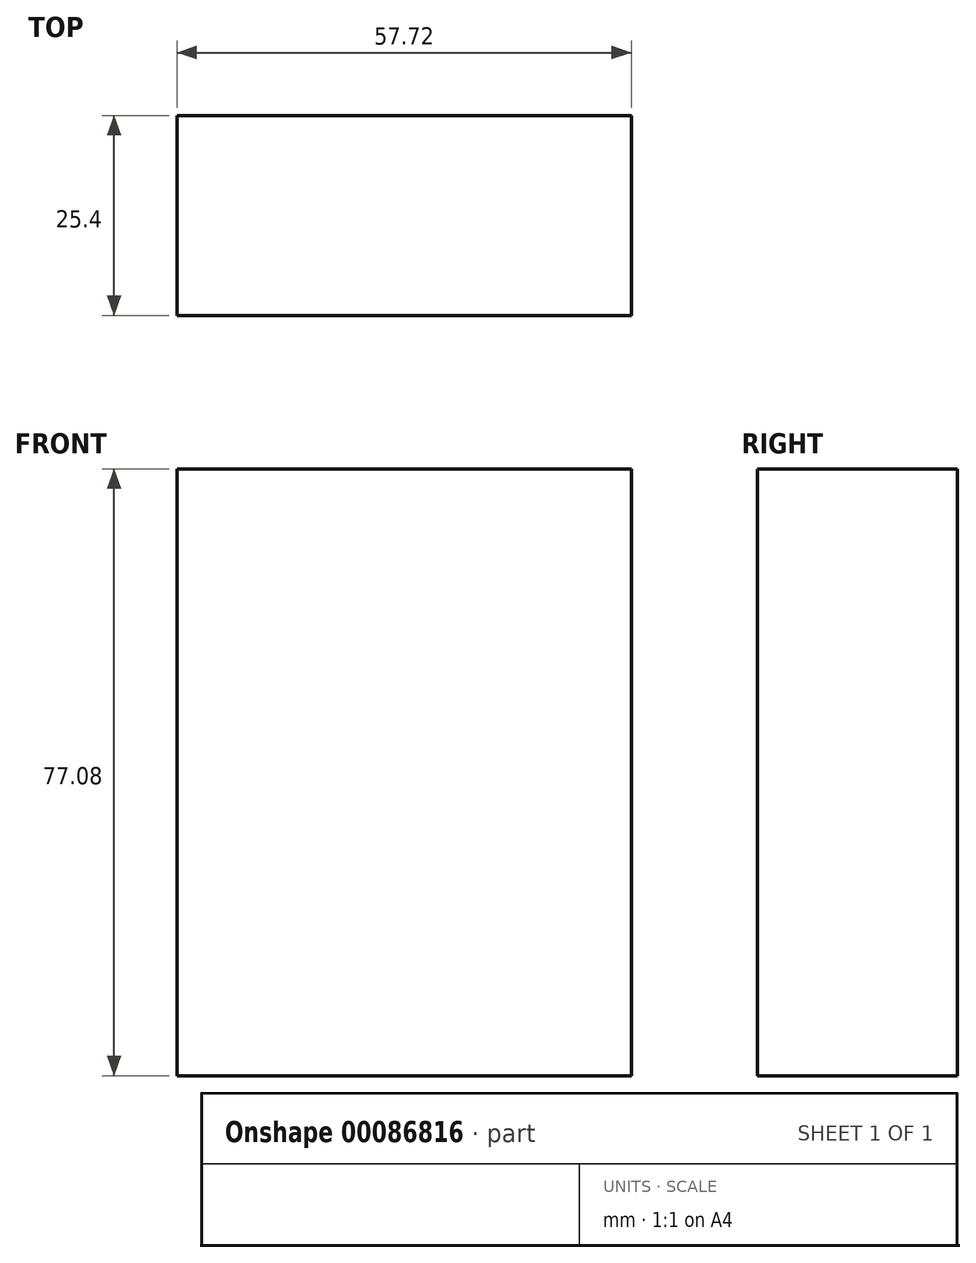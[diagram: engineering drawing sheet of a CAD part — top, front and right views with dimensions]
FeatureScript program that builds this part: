
annotation { "Feature Type Name" : "Feature", "Feature Type Description" : "" }
export const myFeature = defineFeature(function(context is Context, id is Id, definition is map)
    precondition{}
    {
        {
            var Q0;
            Q0=qCreatedBy(makeId("Front.planeOp"),FACE);
            var sketch = newSketch(context, id + "F0", { "sketchPlane" : qUnion([Q0])});
            skLineSegment(sketch, "E0.bottom", {"start": v(-28.86, -38.54) * mm, "end": v(28.86, -38.54) * mm});
            skLineSegment(sketch, "E0.top", {"start": v(-28.86, 38.54) * mm, "end": v(28.86, 38.54) * mm});
            skLineSegment(sketch, "E0.left", {"start": v(-28.86, -38.54) * mm, "end": v(-28.86, 38.54) * mm});
            skLineSegment(sketch, "E0.right", {"start": v(28.86, -38.54) * mm, "end": v(28.86, 38.54) * mm});
            skPoint(sketch, "E0.middle", {"position": v(0, 0) * mm});
            skSolve(sketch);
        }
        {
            var Q0;
            Q0 = qSketchRegion(id + "F0", true);
            extrude(context, id + "F1", {"entities" : qUnion([Q0]), "endBound" : BoundingType.SYMMETRIC, "depth" : 25.4 * mm});
        }
    });
